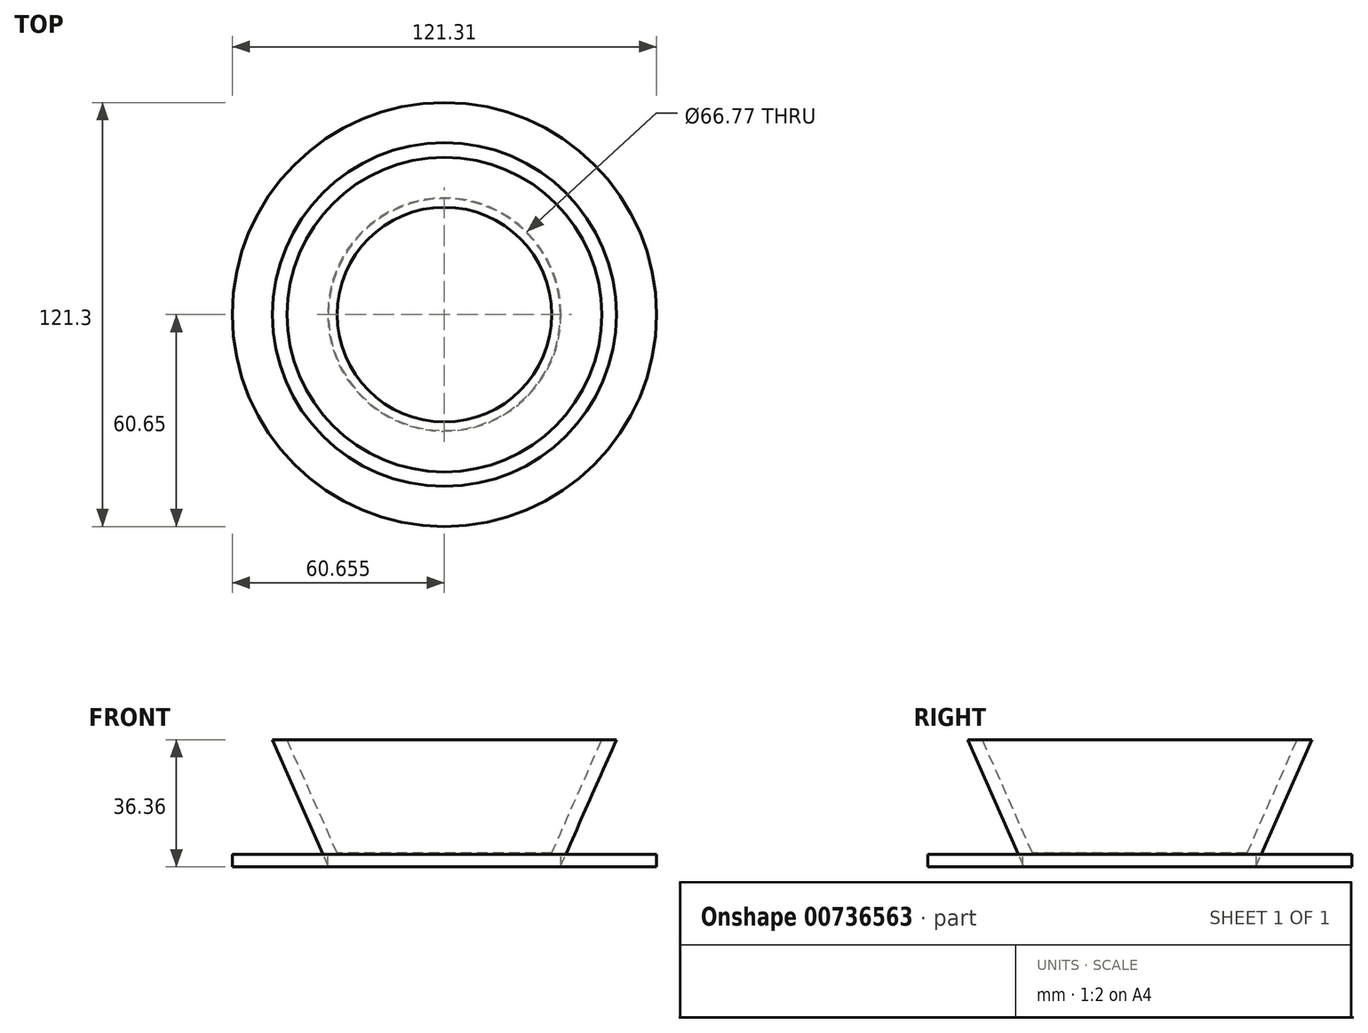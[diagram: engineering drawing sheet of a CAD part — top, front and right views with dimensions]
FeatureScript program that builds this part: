
annotation { "Feature Type Name" : "Feature", "Feature Type Description" : "" }
export const myFeature = defineFeature(function(context is Context, id is Id, definition is map)
    precondition{}
    {
        {
            var Q0;
            Q0=qCreatedBy(makeId("Front.planeOp"),FACE);
            var sketch = newSketch(context, id + "F0", { "sketchPlane" : qUnion([Q0])});
            skLineSegment(sketch, "E0", {"start": v(-45, 36.36) * mm, "end": v(-30.69, 3.96) * mm});
            skLineSegment(sketch, "E1", {"start": v(-30.69, 3.96) * mm, "end": v(0, 3.96) * mm});
            skLineSegment(sketch, "E2.0", {"start": v(-33.17, 0.15) * mm, "end": v(0, 0.15) * mm});
            skLineSegment(sketch, "E2.1", {"start": v(-49.16, 36.36) * mm, "end": v(-33.17, 0.15) * mm});
            skLineSegment(sketch, "E3", {"start": v(0, 3.96) * mm, "end": v(0, 0.15) * mm});
            skLineSegment(sketch, "E4", {"start": v(-45, 36.36) * mm, "end": v(-49.16, 36.36) * mm});
            skPoint(sketch, "E5.orphan", {"position": v(-49.54, 37.2) * mm});
            skPoint(sketch, "E6.orphan", {"position": v(-49.54, 36.36) * mm});
            skSolve(sketch);
        }
        {
            var Q0;
            Q0=qCreatedBy(makeId("Front.planeOp"),FACE);
            var sketch = newSketch(context, id + "F1", { "sketchPlane" : qUnion([Q0])});
            skLineSegment(sketch, "E7.bottom", {"start": v(-33.38, 0) * mm, "end": v(-60.65, 0) * mm});
            skLineSegment(sketch, "E7.top", {"start": v(-33.38, 3.62) * mm, "end": v(-60.65, 3.62) * mm});
            skLineSegment(sketch, "E7.left", {"start": v(-33.38, 0) * mm, "end": v(-33.38, 3.62) * mm});
            skLineSegment(sketch, "E7.right", {"start": v(-60.65, 0) * mm, "end": v(-60.65, 3.62) * mm});
            skSolve(sketch);
        }
        {
            var Q0;
            Q0=makeQuery(id+"F0.imprint","IMPRINT",FACE,{"disambiguationData":[TD([[makeQuery(id+"F0.imprint","IMPRINT",EDGE,{"derivedFrom":sQuery(id+"F0.wireOp",EDGE,"E0")}),-1.0]])]});
            var Q1;
            Q1 = qSketchRegion(id + "F1", true);
            var Q2;
            Q2=sQuery(id+"F0.wireOp",EDGE,"E3");
            revolve(context, id + "F2", {"surfaceOperationType" : NewSurfaceOperationType.NEW, "entities" : qUnion([Q0, Q1]), "axis" : qUnion([Q2]), "revolveType" : RevolveType.FULL});
        }
    });
